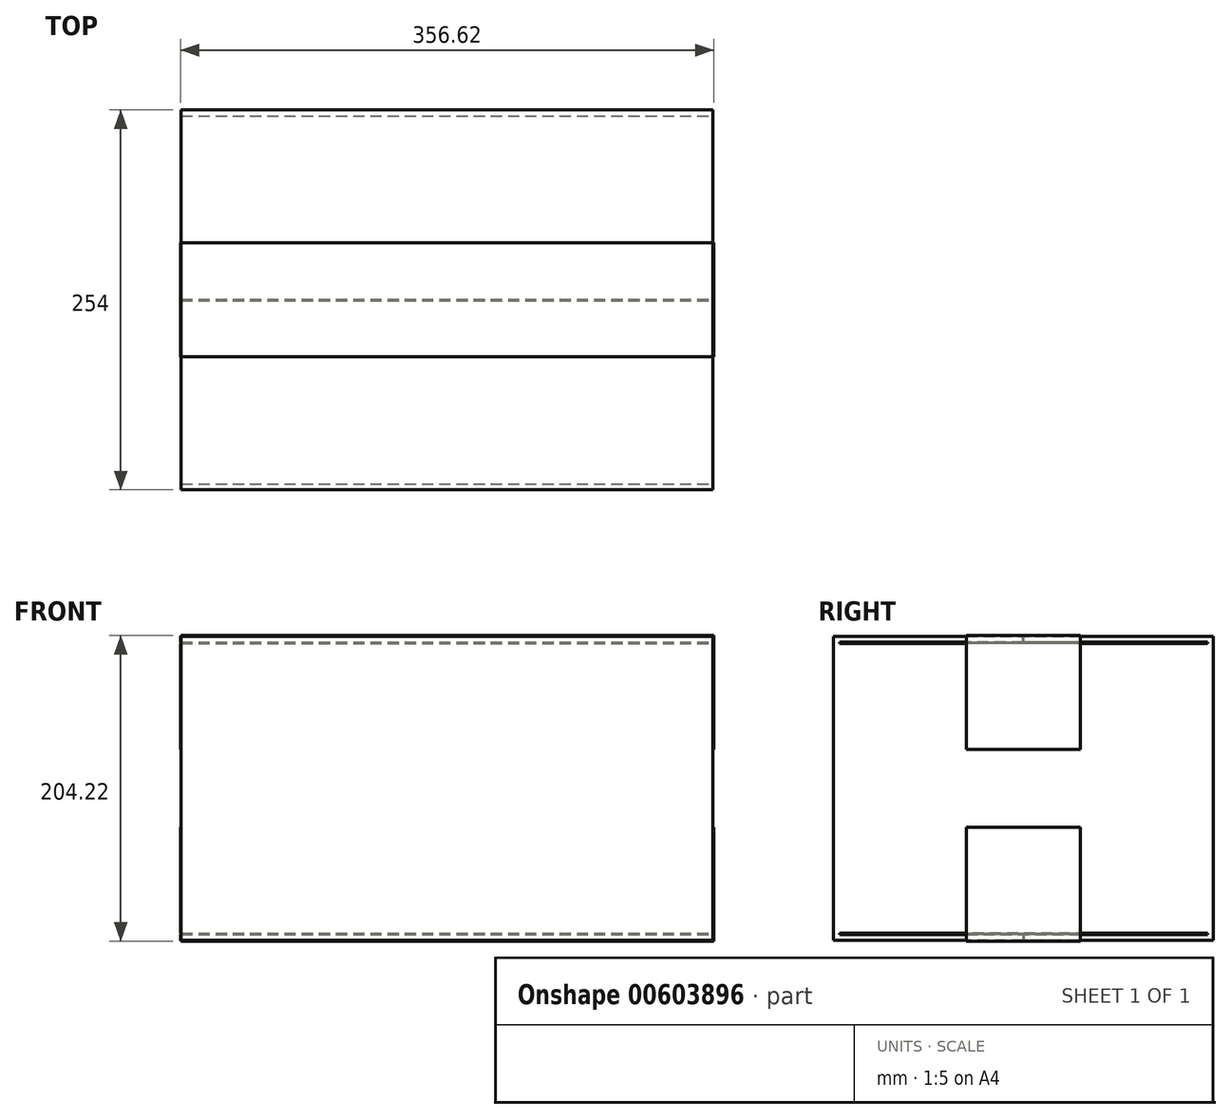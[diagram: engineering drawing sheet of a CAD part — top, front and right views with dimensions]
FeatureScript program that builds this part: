
annotation { "Feature Type Name" : "Feature", "Feature Type Description" : "" }
export const myFeature = defineFeature(function(context is Context, id is Id, definition is map)
    precondition{}
    {
        {
            var Q0;
            Q0=qCreatedBy(makeId("Top.planeOp"),FACE);
            var sketch = newSketch(context, id + "F0", { "sketchPlane" : qUnion([Q0])});
            skLineSegment(sketch, "E0.bottom", {"start": v(177.8, 127) * mm, "end": v(-177.8, 127) * mm});
            skLineSegment(sketch, "E0.top", {"start": v(177.8, -127) * mm, "end": v(-177.8, -127) * mm});
            skLineSegment(sketch, "E0.left", {"start": v(177.8, 127) * mm, "end": v(177.8, -127) * mm});
            skLineSegment(sketch, "E0.right", {"start": v(-177.8, 127) * mm, "end": v(-177.8, -127) * mm});
            skPoint(sketch, "E0.middle", {"position": v(0, 0) * mm});
            skSolve(sketch);
        }
        {
            var Q0;
            Q0=makeQuery(id+"F0.imprint","IMPRINT",FACE,{"disambiguationData":[TD([[makeQuery(id+"F0.imprint","IMPRINT",EDGE,{"derivedFrom":sQuery(id+"F0.wireOp",EDGE,"E0.bottom")}),1.0]])]});
            extrude(context, id + "F1", {"entities" : qUnion([Q0]), "depth" : 203.2 * mm, "offsetDistance" : 25.4 * mm});
        }
        {
            var Q0;
            Q0=makeQuery(id+"F1.opExtrude","CAP_FACE",FACE,{"disambiguationData":[OSD([sQuery(id+"F0.wireOp",EDGE,"E0.bottom"),sQuery(id+"F0.wireOp",EDGE,"E0.top"),sQuery(id+"F0.wireOp",EDGE,"E0.left"),sQuery(id+"F0.wireOp",EDGE,"E0.right")])],"isStart":false});
            var sketch = newSketch(context, id + "F2", { "sketchPlane" : qUnion([Q0])});
            skLineSegment(sketch, "E1.0", {"start": v(-177.8, -0.4) * mm, "end": v(177.8, -0.4) * mm});
            skLineSegment(sketch, "E2.0", {"start": v(-177.8, 0.4) * mm, "end": v(177.8, 0.4) * mm});
            skSolve(sketch);
        }
        {
            var Q0;
            {var subQ0=sQuery(id+"F2.wireOp",EDGE,"E1.0");Q0=makeQuery(id+"F2.imprint","IMPRINT",FACE,{"disambiguationData":[TD([[makeQuery(id+"F2.imprint","IMPRINT",EDGE,{"derivedFrom":subQ0}),1.0]])]});}
            extrude(context, id + "F3", {"entities" : qUnion([Q0]), "operationType" : NewBodyOperationType.REMOVE, "oppositeDirection" : true, "depth" : 3.96 * mm, "offsetDistance" : 25.4 * mm});
        }
        {
            var Q0;
            Q0=makeQuery(id+"F1.opExtrude","CAP_FACE",FACE,{"disambiguationData":[OSD([sQuery(id+"F0.wireOp",EDGE,"E0.bottom"),sQuery(id+"F0.wireOp",EDGE,"E0.top"),sQuery(id+"F0.wireOp",EDGE,"E0.left"),sQuery(id+"F0.wireOp",EDGE,"E0.right")])],"isStart":true});
            var sketch = newSketch(context, id + "F4", { "sketchPlane" : qUnion([Q0])});
            skLineSegment(sketch, "E3.0", {"start": v(-177.8, -0.4) * mm, "end": v(177.8, -0.4) * mm});
            skLineSegment(sketch, "E4.0", {"start": v(-177.8, 0.4) * mm, "end": v(177.8, 0.4) * mm});
            skPoint(sketch, "E5.end.orphan", {"position": v(177.8, 0) * mm});
            skPoint(sketch, "E5.start.orphan", {"position": v(-177.8, 0) * mm});
            skSolve(sketch);
        }
        {
            var Q0;
            Q0 = qSketchRegion(id + "F4", true);
            var Q1;
            {var subQ0=sQuery(id+"F4.wireOp",EDGE,"E3.0");Q1=makeQuery(id+"F4.imprint","IMPRINT",FACE,{"disambiguationData":[TD([[makeQuery(id+"F4.imprint","IMPRINT",EDGE,{"derivedFrom":subQ0}),1.0]])]});}
            extrude(context, id + "F5", {"entities" : qUnion([Q0, Q1]), "operationType" : NewBodyOperationType.REMOVE, "oppositeDirection" : true, "depth" : 3.96 * mm, "offsetDistance" : 25.4 * mm});
        }
        {
            var Q0;
            {var subQ0=sQuery(id+"F0.wireOp",EDGE,"E0.top");var subQ1=sQuery(id+"F0.wireOp",EDGE,"E0.left");var subQ2=sQuery(id+"F0.wireOp",EDGE,"E0.right");Q0=makeQuery(id+"F3.boolean.opBoolean","SPLIT",FACE,{"disambiguationData":[TD([makeQuery(id+"F1.opExtrude","SWEPT_FACE",FACE,{"disambiguationData":[OSD([subQ0])]})])],"derivedFrom":makeQuery(id+"F1.opExtrude","CAP_FACE",FACE,{"disambiguationData":[OSD([sQuery(id+"F0.wireOp",EDGE,"E0.bottom"),subQ0,subQ1,subQ2])],"isStart":false})});}
            var sketch = newSketch(context, id + "F6", { "sketchPlane" : qUnion([Q0])});
            skLineSegment(sketch, "E6.bottom", {"start": v(177.8, -38.1) * mm, "end": v(-177.8, -38.1) * mm});
            skLineSegment(sketch, "E6.top", {"start": v(177.8, 38.1) * mm, "end": v(-177.8, 38.1) * mm});
            skLineSegment(sketch, "E6.left", {"start": v(177.8, -38.1) * mm, "end": v(177.8, 38.1) * mm});
            skLineSegment(sketch, "E6.right", {"start": v(-177.8, -38.1) * mm, "end": v(-177.8, 38.1) * mm});
            skPoint(sketch, "E6.middle", {"position": v(0, 0) * mm});
            skSolve(sketch);
        }
        {
            var Q0;
            Q0 = qSketchRegion(id + "F6", true);
            extrude(context, id + "F7", {"entities" : qUnion([Q0]), "depth" : 0.5 * mm, "offsetDistance" : 25.4 * mm});
        }
        {
            var Q0;
            Q0=makeQuery(id+"F7.opExtrude","SWEPT_FACE",FACE,{"disambiguationData":[OSD([sQuery(id+"F6.wireOp",EDGE,"E6.left")])]});
            var sketch = newSketch(context, id + "F8", { "sketchPlane" : qUnion([Q0])});
            skLineSegment(sketch, "E7.bottom", {"start": v(-38.1, 203.7) * mm, "end": v(38.1, 203.7) * mm});
            skLineSegment(sketch, "E7.top", {"start": v(-38.1, 127.5) * mm, "end": v(38.1, 127.5) * mm});
            skLineSegment(sketch, "E7.left", {"start": v(-38.1, 203.7) * mm, "end": v(-38.1, 127.5) * mm});
            skLineSegment(sketch, "E7.right", {"start": v(38.1, 203.7) * mm, "end": v(38.1, 127.5) * mm});
            skSolve(sketch);
        }
        {
            var Q0;
            Q0 = qSketchRegion(id + "F8", true);
            extrude(context, id + "F9", {"entities" : qUnion([Q0]), "depth" : 0.5 * mm, "offsetDistance" : 25.4 * mm});
        }
        {
            var Q0;
            Q0=makeQuery(id+"F7.opExtrude","SWEPT_FACE",FACE,{"disambiguationData":[OSD([sQuery(id+"F6.wireOp",EDGE,"E6.right")])]});
            var sketch = newSketch(context, id + "F10", { "sketchPlane" : qUnion([Q0])});
            skLineSegment(sketch, "E8.bottom", {"start": v(-38.1, 203.7) * mm, "end": v(38.1, 203.7) * mm});
            skLineSegment(sketch, "E8.top", {"start": v(-38.1, 127.5) * mm, "end": v(38.1, 127.5) * mm});
            skLineSegment(sketch, "E8.left", {"start": v(-38.1, 203.7) * mm, "end": v(-38.1, 127.5) * mm});
            skLineSegment(sketch, "E8.right", {"start": v(38.1, 203.7) * mm, "end": v(38.1, 127.5) * mm});
            skSolve(sketch);
        }
        {
            var Q0;
            {var subQ0=sQuery(id+"F10.wireOp",EDGE,"E8.top");Q0=makeQuery(id+"F10.imprint","IMPRINT",FACE,{"disambiguationData":[TD([[makeQuery(id+"F10.imprint","IMPRINT",EDGE,{"derivedFrom":subQ0}),1.0]])]});}
            extrude(context, id + "F11", {"entities" : qUnion([Q0]), "depth" : 0.5 * mm, "offsetDistance" : 25.4 * mm});
        }
        {
            var Q0;
            Q0=qCreatedBy(makeId("Top.planeOp"),FACE);
            cPlane(context, id + "F12", {"entities" : qUnion([Q0]), "cplaneType" : CPlaneType.OFFSET, "offset" : 101.6 * mm, "width" : 152.4 * mm, "height" : 152.4 * mm});
        }
        {
            var Q0;
            Q0=makeQuery(id+"F11.opExtrude","SWEPT_BODY",BODY,{"disambiguationData":[OSD([sQuery(id+"F6.wireOp",EDGE,"E6.right"),sQuery(id+"F10.wireOp",EDGE,"E8.top"),sQuery(id+"F10.wireOp",EDGE,"E8.left"),sQuery(id+"F10.wireOp",EDGE,"E8.right")])]});
            var Q1;
            Q1=makeQuery(id+"F9.opExtrude","SWEPT_BODY",BODY,{"disambiguationData":[OSD([sQuery(id+"F8.wireOp",EDGE,"E7.bottom"),sQuery(id+"F8.wireOp",EDGE,"E7.top"),sQuery(id+"F8.wireOp",EDGE,"E7.left"),sQuery(id+"F8.wireOp",EDGE,"E7.right")])]});
            var Q2;
            Q2=makeQuery(id+"F7.opExtrude","SWEPT_BODY",BODY,{"disambiguationData":[OSD([sQuery(id+"F6.wireOp",EDGE,"E6.bottom"),sQuery(id+"F6.wireOp",EDGE,"E6.top"),sQuery(id+"F6.wireOp",EDGE,"E6.left"),sQuery(id+"F6.wireOp",EDGE,"E6.right")])]});
            var Q3;
            Q3=qCreatedBy(id+"F12.planeOp",FACE);
            mirror(context, id + "F13", {"entities" : qUnion([Q0, Q1, Q2]), "mirrorPlane" : qUnion([Q3])});
        }
        {
            var Q0;
            Q0=makeQuery(id+"F1.opExtrude","SWEPT_FACE",FACE,{"disambiguationData":[OSD([sQuery(id+"F0.wireOp",EDGE,"E0.left")])]});
            var sketch = newSketch(context, id + "F14", { "sketchPlane" : qUnion([Q0])});
            skLineSegment(sketch, "E9.bottom", {"start": v(123.04, 198.44) * mm, "end": v(-123.04, 198.44) * mm});
            skLineSegment(sketch, "E9.top", {"start": v(123.04, 199.24) * mm, "end": v(-123.04, 199.24) * mm});
            skLineSegment(sketch, "E9.left", {"start": v(123.04, 198.44) * mm, "end": v(123.04, 199.24) * mm});
            skLineSegment(sketch, "E9.right", {"start": v(-123.04, 198.44) * mm, "end": v(-123.04, 199.24) * mm});
            skPoint(sketch, "E9.middle", {"position": v(0, 198.84) * mm});
            skPoint(sketch, "E9.middle.positionSnap0", {"position": v(0, 199.24) * mm});
            skPoint(sketch, "E9.centerSnap0", {"position": v(0, 199.24) * mm});
            skLineSegment(sketch, "E10", {"start": v(-127, 101.6) * mm, "end": v(-92.27, 101.6) * mm, "construction": true});
            skLineSegment(sketch, "E11.MirrorCS", {"start": v(123.04, 4.76) * mm, "end": v(123.04, 3.96) * mm});
            skPoint(sketch, "E12.MirrorP", {"position": v(0, 4.36) * mm});
            skLineSegment(sketch, "E13.MirrorCS", {"start": v(-123.04, 4.76) * mm, "end": v(-123.04, 3.96) * mm});
            skPoint(sketch, "E14.MirrorP", {"position": v(0, 3.96) * mm});
            skLineSegment(sketch, "E15.MirrorCS", {"start": v(123.04, 4.76) * mm, "end": v(-123.04, 4.76) * mm});
            skLineSegment(sketch, "E16.MirrorCS", {"start": v(123.04, 3.96) * mm, "end": v(-123.04, 3.96) * mm});
            skSolve(sketch);
        }
        {
            var Q0;
            Q0 = qSketchRegion(id + "F14", true);
            extrude(context, id + "F15", {"entities" : qUnion([Q0]), "operationType" : NewBodyOperationType.REMOVE, "endBound" : BoundingType.THROUGH_ALL, "oppositeDirection" : true, "depth" : 25.4 * mm, "offsetDistance" : 25.4 * mm});
        }
    });
